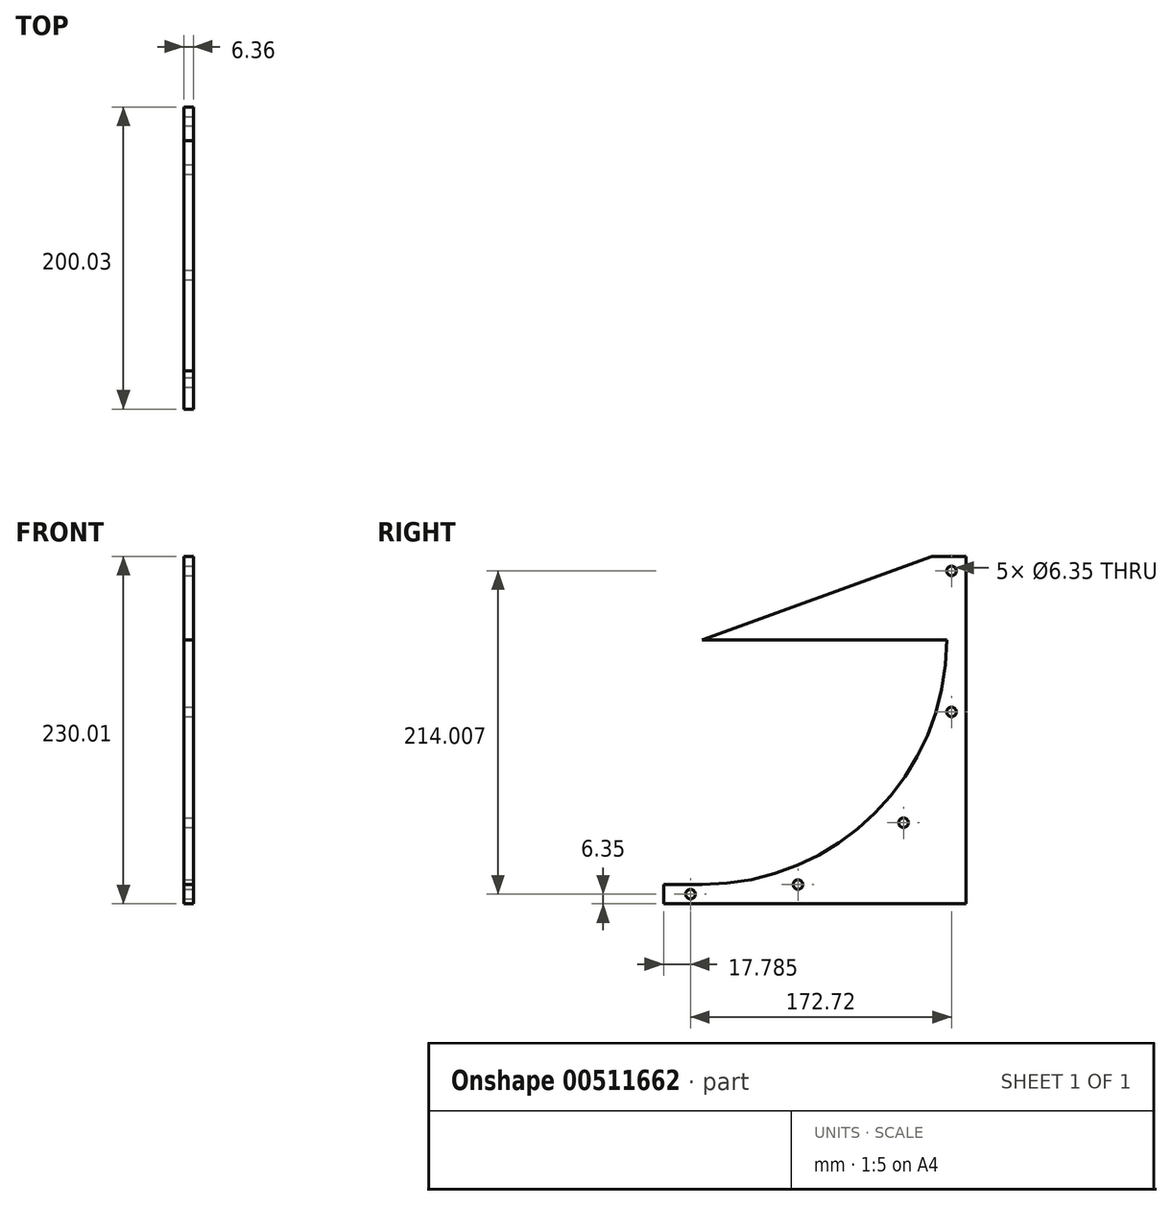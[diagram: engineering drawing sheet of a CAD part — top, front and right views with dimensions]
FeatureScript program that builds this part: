
annotation { "Feature Type Name" : "Feature", "Feature Type Description" : "" }
export const myFeature = defineFeature(function(context is Context, id is Id, definition is map)
    precondition{}
    {
        {
            var Q0;
            Q0=qCreatedBy(makeId("Front.planeOp"),FACE);
            var sketch = newSketch(context, id + "F0", { "sketchPlane" : qUnion([Q0])});
            skLineSegment(sketch, "E0.bottom", {"start": v(-3.17, 127) * mm, "end": v(3.18, 127) * mm});
            skLineSegment(sketch, "E0.top", {"start": v(-3.18, -127) * mm, "end": v(3.17, -127) * mm});
            skLineSegment(sketch, "E0.left", {"start": v(-3.17, 127) * mm, "end": v(-3.18, -127) * mm});
            skLineSegment(sketch, "E0.right", {"start": v(3.18, 127) * mm, "end": v(3.17, -127) * mm});
            skPoint(sketch, "E0.middle", {"position": v(0, 0) * mm});
            skSolve(sketch);
        }
        {
            var Q0;
            Q0=makeQuery(id+"F0.imprint","IMPRINT",FACE,{"disambiguationData":[TD([[makeQuery(id+"F0.imprint","IMPRINT",EDGE,{"derivedFrom":sQuery(id+"F0.wireOp",EDGE,"E0.bottom")}),-1.0]])]});
            extrude(context, id + "F1", {"entities" : qUnion([Q0]), "depth" : 279.4 * mm, "offsetDistance" : 25.4 * mm});
        }
        {
            var Q0;
            Q0=makeQuery(id+"F1.opExtrude","SWEPT_FACE",FACE,{"disambiguationData":[OSD([sQuery(id+"F0.wireOp",EDGE,"E0.left")])]});
            var sketch = newSketch(context, id + "F2", { "sketchPlane" : qUnion([Q0])});
            skArc(sketch, "E1", {"start": v(22.47, 103) * mm, "mid": v(41.98, -45.25) * mm, "end": v(174.63, -114.3) * mm});
            skLineSegment(sketch, "E2.0.0", {"start": v(0, 103) * mm, "end": v(0, -127) * mm});
            skLineSegment(sketch, "E2.0.1", {"start": v(0, -127) * mm, "end": v(279.4, -127) * mm});
            skLineSegment(sketch, "E2.0.2", {"start": v(279.4, -127) * mm, "end": v(279.4, 127) * mm});
            skLineSegment(sketch, "E3", {"start": v(174.63, -114.3) * mm, "end": v(279.4, -114.3) * mm});
            skLineSegment(sketch, "E4", {"start": v(0, 103) * mm, "end": v(22.47, 103) * mm});
            skLineSegment(sketch, "E5", {"start": v(174.62, 47.63) * mm, "end": v(22.47, 103) * mm});
            skLineSegment(sketch, "E6", {"start": v(22.47, 103) * mm, "end": v(174.62, 47.63) * mm});
            skLineSegment(sketch, "E7", {"start": v(174.62, 47.63) * mm, "end": v(0, 47.62) * mm});
            skPoint(sketch, "E2.0.3.end.orphan", {"position": v(0, 127) * mm});
            skSolve(sketch);
        }
        {
            var Q0;
            {var subQ1=sQuery(id+"F2.wireOp",EDGE,"E3");Q0=makeQuery(id+"F2.imprint","IMPRINT",FACE,{"disambiguationData":[TD([[makeQuery(id+"F2.imprint","IMPRINT",EDGE,{"derivedFrom":subQ1}),1.0]])]});}
            var Q1;
            {var subQ0=sQuery(id+"F2.wireOp",EDGE,"E6");Q1=makeQuery(id+"F2.imprint","IMPRINT",FACE,{"disambiguationData":[TD([[makeQuery(id+"F2.imprint","IMPRINT",EDGE,{"derivedFrom":subQ0}),-1.0]])]});}
            extrude(context, id + "F3", {"entities" : qUnion([Q0, Q1]), "operationType" : NewBodyOperationType.REMOVE, "oppositeDirection" : true, "depth" : 25.4 * mm, "offsetDistance" : 25.4 * mm});
        }
        {
            var Q0;
            Q0=makeQuery(id+"F1.opExtrude","SWEPT_FACE",FACE,{"disambiguationData":[OSD([sQuery(id+"F0.wireOp",EDGE,"E0.left")])]});
            var sketch = newSketch(context, id + "F4", { "sketchPlane" : qUnion([Q0])});
            skLineSegment(sketch, "E8.0", {"start": v(174.63, -114.3) * mm, "end": v(279.4, -114.3) * mm});
            skLineSegment(sketch, "E9", {"start": v(200.03, -114.3) * mm, "end": v(200.03, -127) * mm});
            skLineSegment(sketch, "E10", {"start": v(200.03, -127) * mm, "end": v(279.4, -127) * mm});
            skLineSegment(sketch, "E11", {"start": v(279.4, -127) * mm, "end": v(279.4, -114.3) * mm});
            skSolve(sketch);
        }
        {
            var Q0;
            {var subQ2=sQuery(id+"F4.wireOp",EDGE,"E9");Q0=makeQuery(id+"F4.imprint","IMPRINT",FACE,{"disambiguationData":[TD([[makeQuery(id+"F4.imprint","IMPRINT",EDGE,{"derivedFrom":subQ2}),1.0]])]});}
            extrude(context, id + "F5", {"entities" : qUnion([Q0]), "operationType" : NewBodyOperationType.REMOVE, "oppositeDirection" : true, "depth" : 25.4 * mm, "offsetDistance" : 25.4 * mm});
        }
        {
            var Q0;
            Q0=makeQuery(id+"F1.opExtrude","SWEPT_FACE",FACE,{"disambiguationData":[OSD([sQuery(id+"F0.wireOp",EDGE,"E0.right")])]});
            var sketch = newSketch(context, id + "F6", { "sketchPlane" : qUnion([Q0])});
            skPoint(sketch, "E12", {"position": v(-182.25, -120.65) * mm});
            skPoint(sketch, "E12.positionSnap0", {"position": v(-200.03, -120.65) * mm});
            skPoint(sketch, "E13", {"position": v(-111.13, -114.3) * mm});
            skPoint(sketch, "E14", {"position": v(-9.53, 93.36) * mm});
            skPoint(sketch, "E15", {"position": v(-9.53, 0) * mm});
            skPoint(sketch, "E16", {"position": v(-41.28, -73.35) * mm});
            skSolve(sketch);
        }
        {
            var Q0;
            Q0=sQuery(id+"F6.wireOp",VERTEX,"E14");
            var Q1;
            Q1=sQuery(id+"F6.wireOp",VERTEX,"E15");
            var Q2;
            Q2=sQuery(id+"F6.wireOp",VERTEX,"E16");
            var Q3;
            Q3=sQuery(id+"F6.wireOp",VERTEX,"E13");
            var Q4;
            Q4=sQuery(id+"F6.wireOp",VERTEX,"E12");
            var Q5;
            Q5=makeQuery(id+"F1.opExtrude","SWEPT_BODY",BODY,{"disambiguationData":[OSD([sQuery(id+"F0.wireOp",EDGE,"E0.bottom"),sQuery(id+"F0.wireOp",EDGE,"E0.top"),sQuery(id+"F0.wireOp",EDGE,"E0.left"),sQuery(id+"F0.wireOp",EDGE,"E0.right")])]});
            hole(context, id + "F7", {"style" : HoleStyle.SIMPLE, "endStyle" : HoleEndStyle.THROUGH, "holeDiameter" : 6.35 * mm, "isTappedThrough" : true, "tappedDepth" : 12.7 * mm, "tapClearance" : 3, "locations" : qUnion([Q0, Q1, Q2, Q3, Q4]), "scope" : qUnion([Q5])});
        }
    });
